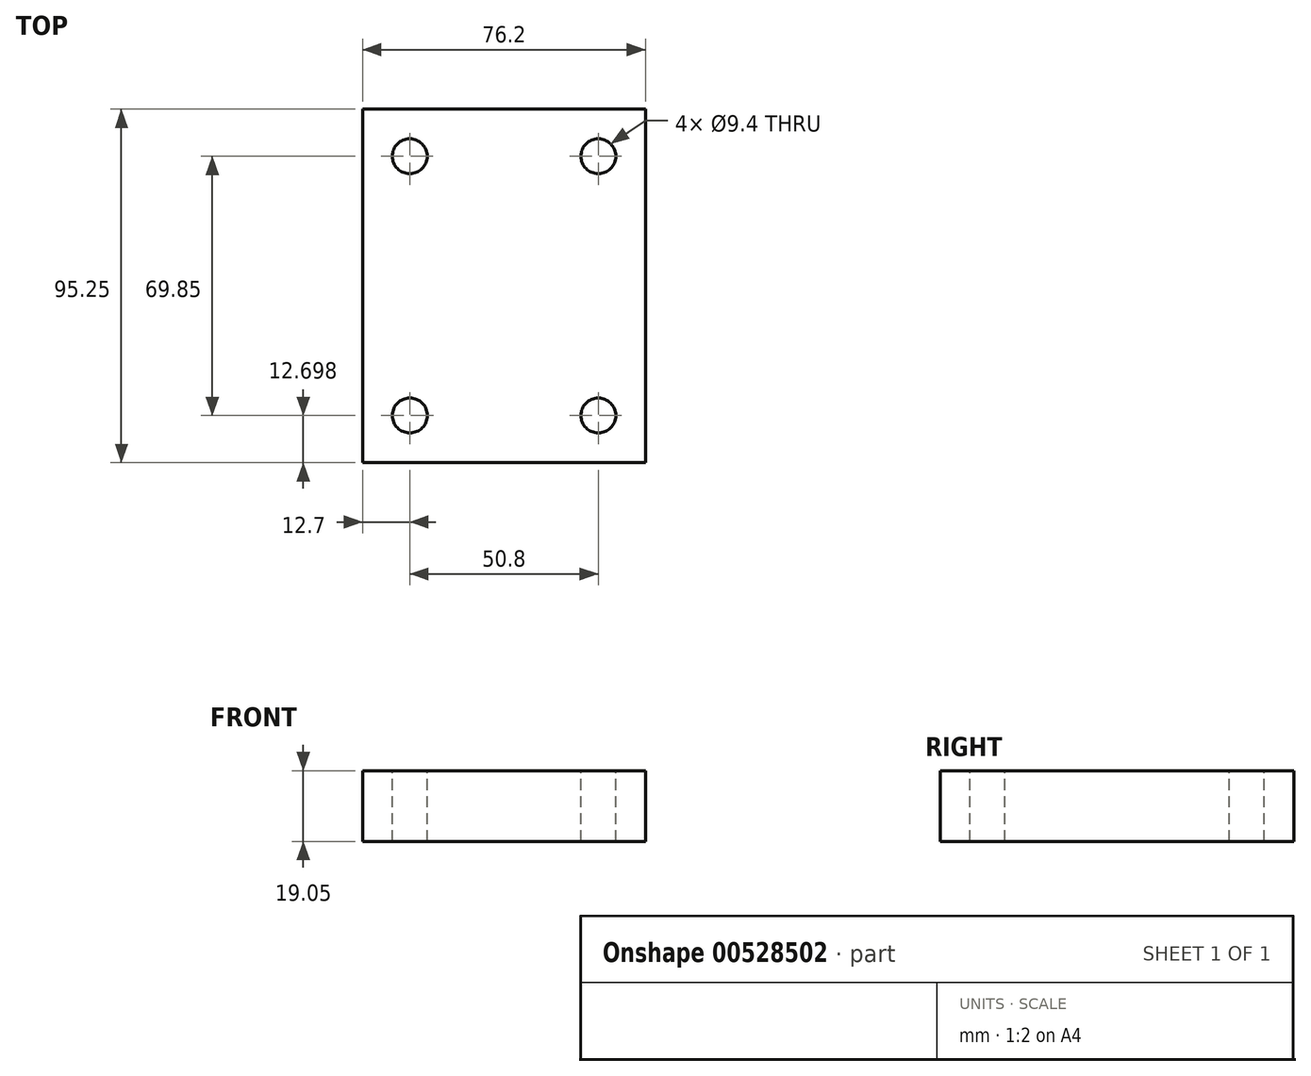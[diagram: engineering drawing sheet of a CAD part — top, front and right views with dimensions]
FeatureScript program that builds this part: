
annotation { "Feature Type Name" : "Feature", "Feature Type Description" : "" }
export const myFeature = defineFeature(function(context is Context, id is Id, definition is map)
    precondition{}
    {
        {
            var Q0;
            Q0=qCreatedBy(makeId("Right.planeOp"),FACE);
            var sketch = newSketch(context, id + "F0", { "sketchPlane" : qUnion([Q0])});
            skLineSegment(sketch, "E0", {"start": v(-39.88, -13.25) * mm, "end": v(55.37, -13.25) * mm});
            skLineSegment(sketch, "E1", {"start": v(-39.88, -13.25) * mm, "end": v(-39.88, 5.8) * mm});
            skLineSegment(sketch, "E2", {"start": v(-39.88, 5.8) * mm, "end": v(55.37, 5.8) * mm});
            skLineSegment(sketch, "E3", {"start": v(55.37, 5.8) * mm, "end": v(55.37, -13.25) * mm});
            skSolve(sketch);
        }
        {
            var Q0;
            Q0=makeQuery(id+"F0.imprint","IMPRINT",FACE,{"disambiguationData":[TD([[makeQuery(id+"F0.imprint","IMPRINT",EDGE,{"derivedFrom":sQuery(id+"F0.wireOp",EDGE,"E0")}),1.0]])]});
            extrude(context, id + "F1", {"entities" : qUnion([Q0]), "depth" : 76.2 * mm, "offsetDistance" : 25.4 * mm});
        }
        {
            var Q0;
            Q0=makeQuery(id+"F1.opExtrude","SWEPT_FACE",FACE,{"disambiguationData":[OSD([sQuery(id+"F0.wireOp",EDGE,"E2")])]});
            var sketch = newSketch(context, id + "F2", { "sketchPlane" : qUnion([Q0])});
            skPoint(sketch, "E4", {"position": v(63.5, -27.18) * mm});
            skCircle(sketch, "E5", {"center": v(63.5, -27.18) * mm, "radius": 4.7 * mm});
            skCircle(sketch, "E6", {"center": v(12.73, -27.18) * mm, "radius": 4.7 * mm});
            skCircle(sketch, "E7", {"center": v(12.7, 42.67) * mm, "radius": 4.7 * mm});
            skPoint(sketch, "E8.end.orphan", {"position": v(63.5, -39.88) * mm});
            skPoint(sketch, "E9.end.orphan", {"position": v(76.2, -27.18) * mm});
            skPoint(sketch, "E9.start.orphan", {"position": v(76.2, -39.88) * mm});
            skPoint(sketch, "E10.end.orphan", {"position": v(12.73, -39.88) * mm});
            skPoint(sketch, "E11.end.orphan", {"position": v(0, -27.18) * mm});
            skPoint(sketch, "E11.start.orphan", {"position": v(0, -39.88) * mm});
            skPoint(sketch, "E12.end.orphan", {"position": v(12.7, 55.37) * mm});
            skPoint(sketch, "E13.end.orphan", {"position": v(0, 42.67) * mm});
            skPoint(sketch, "E13.start.orphan", {"position": v(0, 55.37) * mm});
            skCircle(sketch, "E14", {"center": v(63.5, 42.67) * mm, "radius": 4.7 * mm});
            skPoint(sketch, "E15.end.orphan", {"position": v(76.2, 42.67) * mm});
            skPoint(sketch, "E16.end.orphan", {"position": v(63.5, 55.37) * mm});
            skPoint(sketch, "E16.start.orphan", {"position": v(76.2, 55.37) * mm});
            skSolve(sketch);
        }
        {
            var Q0;
            Q0=makeQuery(id+"F2.imprint","IMPRINT",FACE,{"disambiguationData":[TD([[makeQuery(id+"F2.imprint","IMPRINT",EDGE,{"derivedFrom":sQuery(id+"F2.wireOp",EDGE,"E5")}),1.0]])]});
            var Q1;
            Q1=makeQuery(id+"F2.imprint","IMPRINT",FACE,{"disambiguationData":[TD([[makeQuery(id+"F2.imprint","IMPRINT",EDGE,{"derivedFrom":sQuery(id+"F2.wireOp",EDGE,"E6")}),1.0]])]});
            var Q2;
            Q2=makeQuery(id+"F2.imprint","IMPRINT",FACE,{"disambiguationData":[TD([[makeQuery(id+"F2.imprint","IMPRINT",EDGE,{"derivedFrom":sQuery(id+"F2.wireOp",EDGE,"E7")}),1.0]])]});
            var Q3;
            Q3=makeQuery(id+"F2.imprint","IMPRINT",FACE,{"disambiguationData":[TD([[makeQuery(id+"F2.imprint","IMPRINT",EDGE,{"derivedFrom":sQuery(id+"F2.wireOp",EDGE,"E14")}),1.0]])]});
            var Q4;
            Q4=sQuery(id+"F2.wireOp",EDGE,"E5");
            extrude(context, id + "F3", {"entities" : qUnion([Q0, Q1, Q2, Q3]), "operationType" : NewBodyOperationType.REMOVE, "surfaceEntities" : qUnion([Q4]), "oppositeDirection" : true, "depth" : 25.4 * mm, "offsetDistance" : 25.4 * mm});
        }
        {
            var Q0;
            Q0=makeQuery(id+"F1.opExtrude","CAP_FACE",FACE,{"disambiguationData":[OSD([sQuery(id+"F0.wireOp",EDGE,"E0"),sQuery(id+"F0.wireOp",EDGE,"E1"),sQuery(id+"F0.wireOp",EDGE,"E2"),sQuery(id+"F0.wireOp",EDGE,"E3")])],"isStart":false});
            var sketch = newSketch(context, id + "F4", { "sketchPlane" : qUnion([Q0])});
            skLineSegment(sketch, "E17", {"start": v(-39.88, 5.8) * mm, "end": v(4.57, 5.8) * mm});
            skSolve(sketch);
        }
    });
